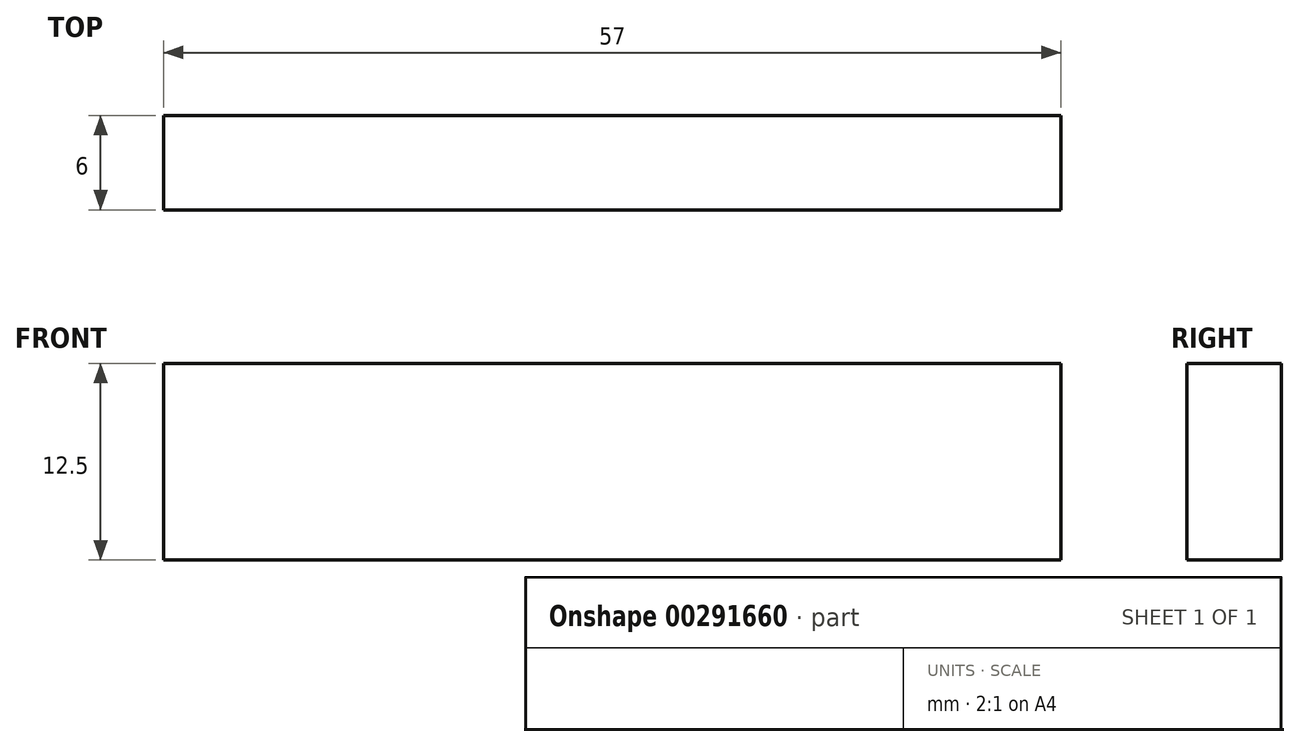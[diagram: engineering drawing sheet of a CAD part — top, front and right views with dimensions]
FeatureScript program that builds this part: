
annotation { "Feature Type Name" : "Feature", "Feature Type Description" : "" }
export const myFeature = defineFeature(function(context is Context, id is Id, definition is map)
    precondition{}
    {
        {
            var Q0;
            Q0=qCreatedBy(makeId("Front.planeOp"),FACE);
            var sketch = newSketch(context, id + "F0", { "sketchPlane" : qUnion([Q0])});
            skLineSegment(sketch, "E0.bottom", {"start": v(-57.07, 16.48) * mm, "end": v(-0.07, 16.48) * mm});
            skLineSegment(sketch, "E0.top", {"start": v(-57.07, 3.98) * mm, "end": v(-0.07, 3.98) * mm});
            skLineSegment(sketch, "E0.left", {"start": v(-57.07, 16.48) * mm, "end": v(-57.07, 3.98) * mm});
            skLineSegment(sketch, "E0.right", {"start": v(-0.07, 16.48) * mm, "end": v(-0.07, 3.98) * mm});
            skSolve(sketch);
        }
        {
            var Q0;
            Q0=makeQuery(id+"F0.imprint","IMPRINT",FACE,{"disambiguationData":[TD([[makeQuery(id+"F0.imprint","IMPRINT",EDGE,{"derivedFrom":sQuery(id+"F0.wireOp",EDGE,"E0.bottom")}),-1.0]])]});
            extrude(context, id + "F1", {"entities" : qUnion([Q0]), "endBound" : BoundingType.SYMMETRIC, "depth" : 6 * mm});
        }
    });
